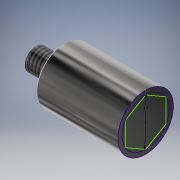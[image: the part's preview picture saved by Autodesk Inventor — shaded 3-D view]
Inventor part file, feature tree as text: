
AUTODESK INVENTOR PART (.ipt)
format: ipt  version: 2018 (Build 220112000, 112)  size: 140,800 bytes
history: native  units: mm
features: chamfer x2, revolve x1, thread x1, extrude x1, sketch x1
ambient origin geometry x8: Origin, YZ Plane, XZ Plane, XY Plane, X Axis, Y Axis, Z Axis, Center Point
bodies: Solido1 (feature_tree)
feature tree (6):
  revolve  "Rivoluzione1"
  chamfer  "Smusso1"  Distance=8.0mm
  thread  "Filettatura1"
  chamfer  "Smusso2"  Distance=10.0mm
  extrude  "Estrusione2"  Depth=20.0mm
  sketch  "Schizzo2"
